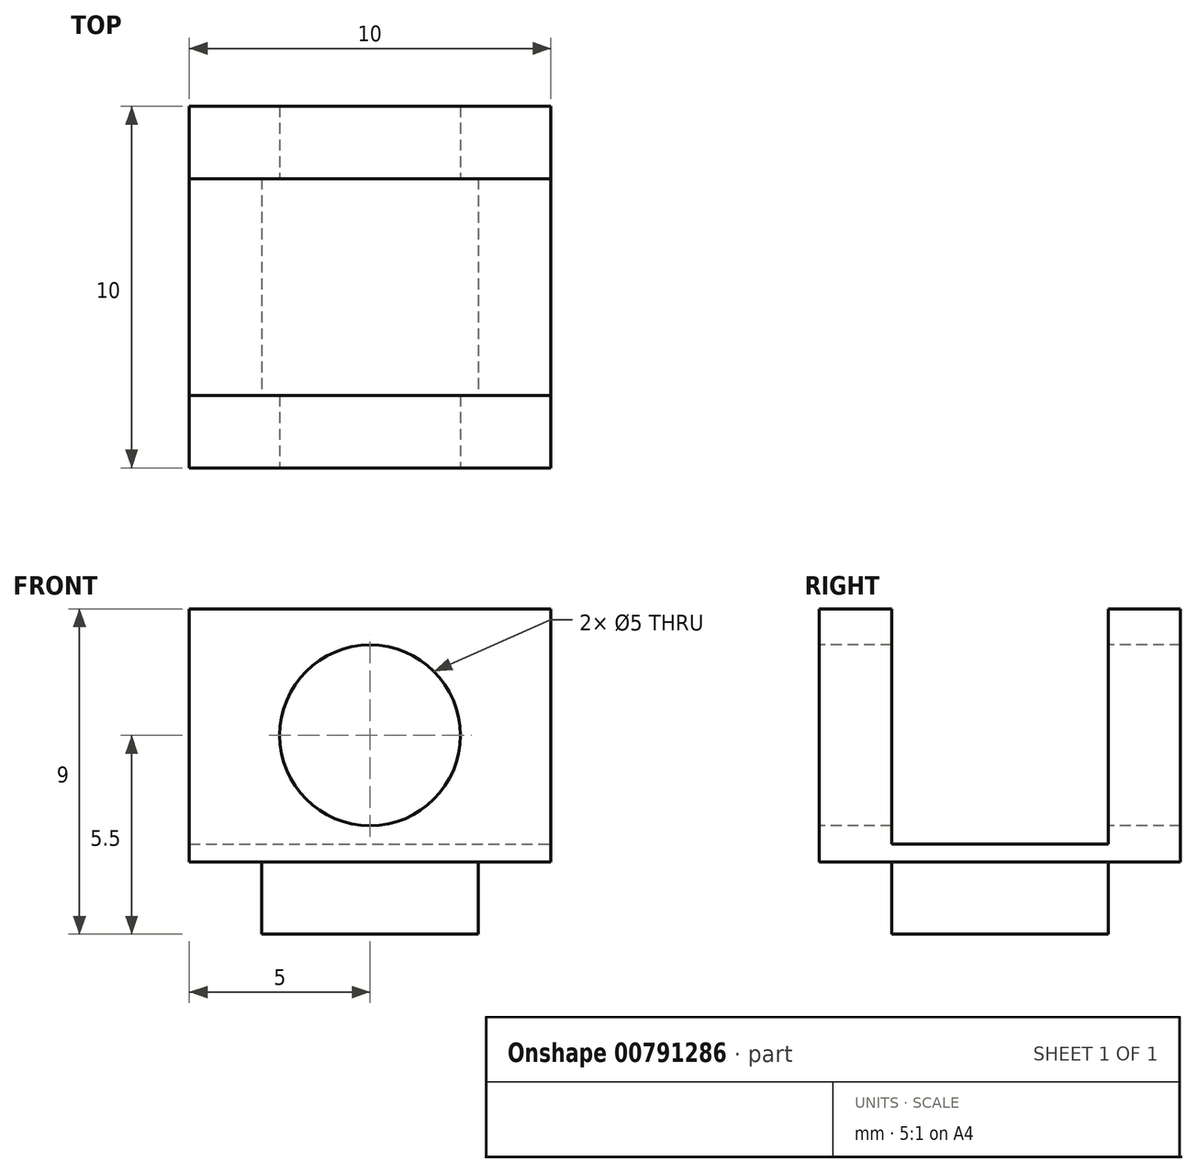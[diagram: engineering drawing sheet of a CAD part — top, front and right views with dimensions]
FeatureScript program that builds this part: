
annotation { "Feature Type Name" : "Feature", "Feature Type Description" : "" }
export const myFeature = defineFeature(function(context is Context, id is Id, definition is map)
    precondition{}
    {
        {
            var Q0;
            Q0=qCreatedBy(makeId("Top.planeOp"),FACE);
            var sketch = newSketch(context, id + "F0", { "sketchPlane" : qUnion([Q0])});
            skLineSegment(sketch, "E0.bottom", {"start": v(5, 5) * mm, "end": v(-5, 5) * mm});
            skLineSegment(sketch, "E0.top", {"start": v(5, -5) * mm, "end": v(-5, -5) * mm});
            skLineSegment(sketch, "E0.left", {"start": v(5, 5) * mm, "end": v(5, -5) * mm});
            skLineSegment(sketch, "E0.right", {"start": v(-5, 5) * mm, "end": v(-5, -5) * mm});
            skPoint(sketch, "E0.middle", {"position": v(0, 0) * mm});
            skLineSegment(sketch, "E1.bottom", {"start": v(3, 3) * mm, "end": v(-3, 3) * mm});
            skLineSegment(sketch, "E1.top", {"start": v(3, -3) * mm, "end": v(-3, -3) * mm});
            skLineSegment(sketch, "E1.left", {"start": v(3, 3) * mm, "end": v(3, -3) * mm});
            skLineSegment(sketch, "E1.right", {"start": v(-3, 3) * mm, "end": v(-3, -3) * mm});
            skLineSegment(sketch, "E2.bottom", {"start": v(3, 3) * mm, "end": v(5, 3) * mm});
            skLineSegment(sketch, "E2.top", {"start": v(3, -3) * mm, "end": v(5, -3) * mm});
            skLineSegment(sketch, "E2.right", {"start": v(5, 3) * mm, "end": v(5, -3) * mm});
            skLineSegment(sketch, "E3.bottom", {"start": v(-3, 3) * mm, "end": v(-5, 3) * mm});
            skLineSegment(sketch, "E3.top", {"start": v(-3, -3) * mm, "end": v(-5, -3) * mm});
            skLineSegment(sketch, "E3.right", {"start": v(-5, 3) * mm, "end": v(-5, -3) * mm});
            skSolve(sketch);
        }
        {
            var Q0;
            Q0=makeQuery(id+"F0.imprint","IMPRINT",FACE,{"disambiguationData":[TD([[makeQuery(id+"F0.imprint","IMPRINT",EDGE,{"derivedFrom":sQuery(id+"F0.wireOp",EDGE,"E1.bottom")}),1.0]])]});
            extrude(context, id + "F1", {"entities" : qUnion([Q0]), "oppositeDirection" : true, "depth" : 2 * mm, "offsetDistance" : 25 * mm});
        }
        {
            var Q0;
            Q0=makeQuery(id+"F0.imprint","IMPRINT",FACE,{"disambiguationData":[TD([[makeQuery(id+"F0.imprint","IMPRINT",EDGE,{"derivedFrom":sQuery(id+"F0.wireOp",EDGE,"E0.bottom")}),1.0]])]});
            var Q1;
            Q1=makeQuery(id+"F0.imprint","IMPRINT",FACE,{"disambiguationData":[TD([[makeQuery(id+"F0.imprint","IMPRINT",EDGE,{"derivedFrom":sQuery(id+"F0.wireOp",EDGE,"E1.bottom")}),1.0]])]});
            var Q2;
            Q2=makeQuery(id+"F0.imprint","IMPRINT",FACE,{"disambiguationData":[TD([[makeQuery(id+"F0.imprint","IMPRINT",EDGE,{"derivedFrom":sQuery(id+"F0.wireOp",EDGE,"E3.bottom")}),1.0]])]});
            var Q3;
            {var subQ1=sQuery(id+"F0.wireOp",EDGE,"E0.top");Q3=makeQuery(id+"F0.imprint","IMPRINT",FACE,{"disambiguationData":[TD([[makeQuery(id+"F0.imprint","IMPRINT",EDGE,{"derivedFrom":subQ1}),-1.0]])]});}
            var Q4;
            Q4=makeQuery(id+"F0.imprint","IMPRINT",FACE,{"disambiguationData":[TD([[makeQuery(id+"F0.imprint","IMPRINT",EDGE,{"derivedFrom":sQuery(id+"F0.wireOp",EDGE,"E2.bottom")}),-1.0]])]});
            extrude(context, id + "F2", {"entities" : qUnion([Q0, Q1, Q2, Q3, Q4]), "operationType" : NewBodyOperationType.ADD, "depth" : 0.5 * mm, "offsetDistance" : 25 * mm});
        }
        {
            var Q0;
            Q0=makeQuery(id+"F2.opExtrude","SWEPT_FACE",FACE,{"disambiguationData":[OSD([sQuery(id+"F0.wireOp",EDGE,"E0.top")])]});
            var sketch = newSketch(context, id + "F3", { "sketchPlane" : qUnion([Q0])});
            skLineSegment(sketch, "E4.bottom", {"start": v(-5, 0.5) * mm, "end": v(5, 0.5) * mm});
            skLineSegment(sketch, "E4.top", {"start": v(-5, 7) * mm, "end": v(5, 7) * mm});
            skLineSegment(sketch, "E4.left", {"start": v(-5, 0.5) * mm, "end": v(-5, 7) * mm});
            skLineSegment(sketch, "E4.right", {"start": v(5, 0.5) * mm, "end": v(5, 7) * mm});
            skLineSegment(sketch, "E5", {"start": v(0, 7) * mm, "end": v(0, 0) * mm});
            skCircle(sketch, "E6", {"center": v(0, 3.5) * mm, "radius": 2.5 * mm});
            skSolve(sketch);
        }
        {
            var Q0;
            {var subQ5=sQuery(id+"F3.wireOp",EDGE,"E4.right");Q0=makeQuery(id+"F3.imprint","IMPRINT",FACE,{"disambiguationData":[TD([[makeQuery(id+"F3.imprint","IMPRINT",EDGE,{"derivedFrom":subQ5}),1.0]])]});}
            var Q1;
            {var subQ0=sQuery(id+"F3.wireOp",EDGE,"E4.left");Q1=makeQuery(id+"F3.imprint","IMPRINT",FACE,{"disambiguationData":[TD([[makeQuery(id+"F3.imprint","IMPRINT",EDGE,{"derivedFrom":subQ0}),-1.0]])]});}
            extrude(context, id + "F4", {"entities" : qUnion([Q0, Q1]), "operationType" : NewBodyOperationType.ADD, "oppositeDirection" : true, "depth" : 10 * mm, "offsetDistance" : 25 * mm});
        }
        {
            var Q0;
            Q0=makeQuery(id+"F4.opExtrude","SWEPT_FACE",FACE,{"disambiguationData":[OSD([sQuery(id+"F3.wireOp",EDGE,"E4.top")])]});
            var sketch = newSketch(context, id + "F5", { "sketchPlane" : qUnion([Q0])});
            skLineSegment(sketch, "E7.bottom", {"start": v(-5, 3) * mm, "end": v(5, 3) * mm});
            skLineSegment(sketch, "E7.top", {"start": v(-5, -3) * mm, "end": v(5, -3) * mm});
            skLineSegment(sketch, "E7.left", {"start": v(-5, 3) * mm, "end": v(-5, -3) * mm});
            skLineSegment(sketch, "E7.right", {"start": v(5, 3) * mm, "end": v(5, -3) * mm});
            skSolve(sketch);
        }
        {
            var Q0;
            Q0=makeQuery(id+"F5.imprint","IMPRINT",FACE,{"disambiguationData":[TD([[makeQuery(id+"F5.imprint","IMPRINT",EDGE,{"derivedFrom":sQuery(id+"F5.wireOp",EDGE,"E7.bottom")}),-1.0]])]});
            extrude(context, id + "F6", {"entities" : qUnion([Q0]), "operationType" : NewBodyOperationType.REMOVE, "oppositeDirection" : true, "depth" : 6.5 * mm, "offsetDistance" : 25 * mm});
        }
    });
